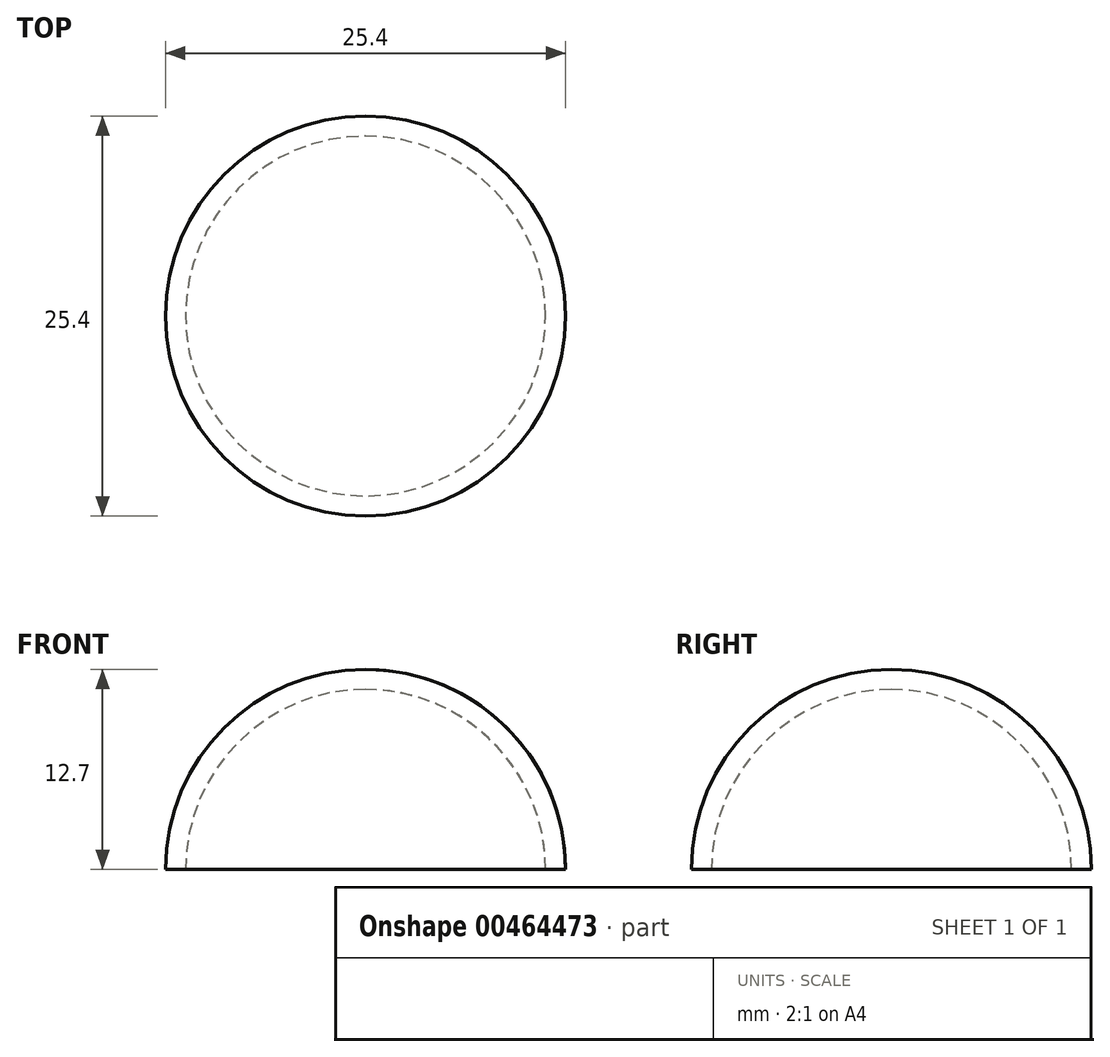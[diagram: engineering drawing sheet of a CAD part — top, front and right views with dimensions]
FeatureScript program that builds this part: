
annotation { "Feature Type Name" : "Feature", "Feature Type Description" : "" }
export const myFeature = defineFeature(function(context is Context, id is Id, definition is map)
    precondition{}
    {
        {
            var Q0;
            Q0=qCreatedBy(makeId("Front.planeOp"),FACE);
            var sketch = newSketch(context, id + "F0", { "sketchPlane" : qUnion([Q0])});
            skArc(sketch, "E0", {"start": v(0, 11.43) * mm, "mid": v(-8.08, 8.08) * mm, "end": v(-11.43, 0) * mm});
            skArc(sketch, "E1", {"start": v(0, 12.7) * mm, "mid": v(-8.98, 8.98) * mm, "end": v(-12.7, 0) * mm});
            skLineSegment(sketch, "E2", {"start": v(-11.43, 0) * mm, "end": v(-12.7, 0) * mm});
            skLineSegment(sketch, "E3", {"start": v(0, 12.7) * mm, "end": v(0, 11.43) * mm});
            skSolve(sketch);
        }
        {
            var Q0;
            Q0 = qSketchRegion(id + "F0", true);
            var Q1;
            Q1=sQuery(id+"F0.wireOp",EDGE,"E3");
            revolve(context, id + "F1", {"entities" : qUnion([Q0]), "axis" : qUnion([Q1]), "revolveType" : RevolveType.FULL});
        }
    });
